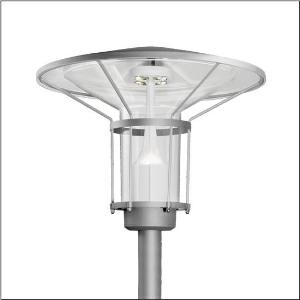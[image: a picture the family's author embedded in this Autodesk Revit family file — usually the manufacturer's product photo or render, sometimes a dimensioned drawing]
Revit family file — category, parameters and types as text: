
# Revit family: laterne_classic_iq___pl1_2s_5xa5245jf14h000022_9e24
name_source: partatom
category: Lighting Fixtures
units: mm (PartAtom-declared; Revit-internal decimal feet)

## family parameters
Cut with Voids When Loaded = No
Host = Face
Light Source = No
Part Type = Normal
Room Calculation Point = No
Round Connector Dimension = Use Diameter
Shared = No

## types (1)
- --- (1 x LED, 2660 lm, 19.3 W, 3000K)
    Apparent Load = 19 VA
    CIE Flux Codes = 21 60 93 97 100
    Color Rendering = 70
    Color Temperature = 3000K
    Default Elevation = 1800 mm
    Description = Lantern Classic iQ, mast luminaire, Module 540 iQ-SR, primary light control with 3 zone facetted reflector, of plastic, silver coated, highly specular, structured, primary optical cover: cover, of PMMA, transparent, light distribution: PL1.2s, light emission: direct distribution, primary light characteristic: symmetric, installation type: post-top, LED, High Power LED, rated luminous flux: 2.660lm, luminous efficacy: 138lm/W, light colour: 730, colour temperature: 3000K, control gear: ECG iQ, control: Street-Remote, Auto-Match, Temp-Guard, Lumen-Switch, Night-Set, Smart-Wire, Light-Fading, Desk-Remote (wireless, voltage-free reading and setting of iQ features in the workshop via application-optimized NFC function/RFID function), optimised constant luminous flux control (CLO 2.0), pre-setting: logarithmic dimming characteristic, mains connection: 230..240V, AC, 50/60Hz, connection cable pre-assembled, cable length: 5,5m, wiring characteristics: H07RN-F, start of lifetime: 19W, end of service life: 21W, reduction: 10W, luminaire housing, upper part, of glass-fibre reinforced polyester, coated, Siteco® metallic grey (DB 702S), diameter: 750mm, height: 596mm, spigot size: d x l = 76 x 70mm (post-top) | with reducer (optional accessory) 60 x 70mm, post-top mast mounting element, of diecast aluminium, coated, Siteco® metallic grey (DB 702S), Module 540 iQ-SR, traffic white (RAL 9016), equipment: standard, protection rating (complete): IP65, insulation class (complete): insulation class II (safety insulation), certification: CE, ENEC, VDE, packaging unit: 1 piece

Light Distribution: PL1.2s
    Height = 596 mm
    Lamp = 1 x LED
    Lamp Light Flux = 2660 lm
    Lamp Power = 19.3 W
    Lamp count = 1
    Length = 750 mm
    Luminous efficacy = 138 lm/W
    Manufacturer = Siteco
    ModVariant = No
    Model = 5XA5245JF14H000022
    Number of Poles = 1
    OnlyDefault = Yes
    Power Factor = 1
    Product Name = Laterne Classic iQ | PL1.2s
    Product group = mast luminaire | pylon top
    ProductGroupID = 6100
    Protection Class = Protection class II
    Protection Degree = IP 65
    RLX_Detail_Level = 1
    RLX_Emergency_Light_Flux = 0 lm
    RLX_Emergency_Type = 0
    RLX_Emergency_Type_DB = No
    RlxData = <blob elided: 62369 chars, md5=7b7f1aee>
    Socket = socket
    Standby Power = 0 W
    System Light Flux = 2660 lm
    System Power = 19 W
    Type Comments = factory setting: luminous flux: 100 % | dim-lin: 254 | 403 mA
    Type Image = l_1006052.jpg
    URL = http://relux.com
    VarID = @adj_115597
    Voltage = 0 V
    Weight = 0.00 kg
    Width = 0 mm  [stored 0 ft]

note: [stored X ft] marks values corroborated as IEEE doubles in the binary element streams (Revit-internal decimal feet)

## geometry (parser evidence)
native form markers: Blend x4, Sweep x9
no freeform markers — native parametric forms only
